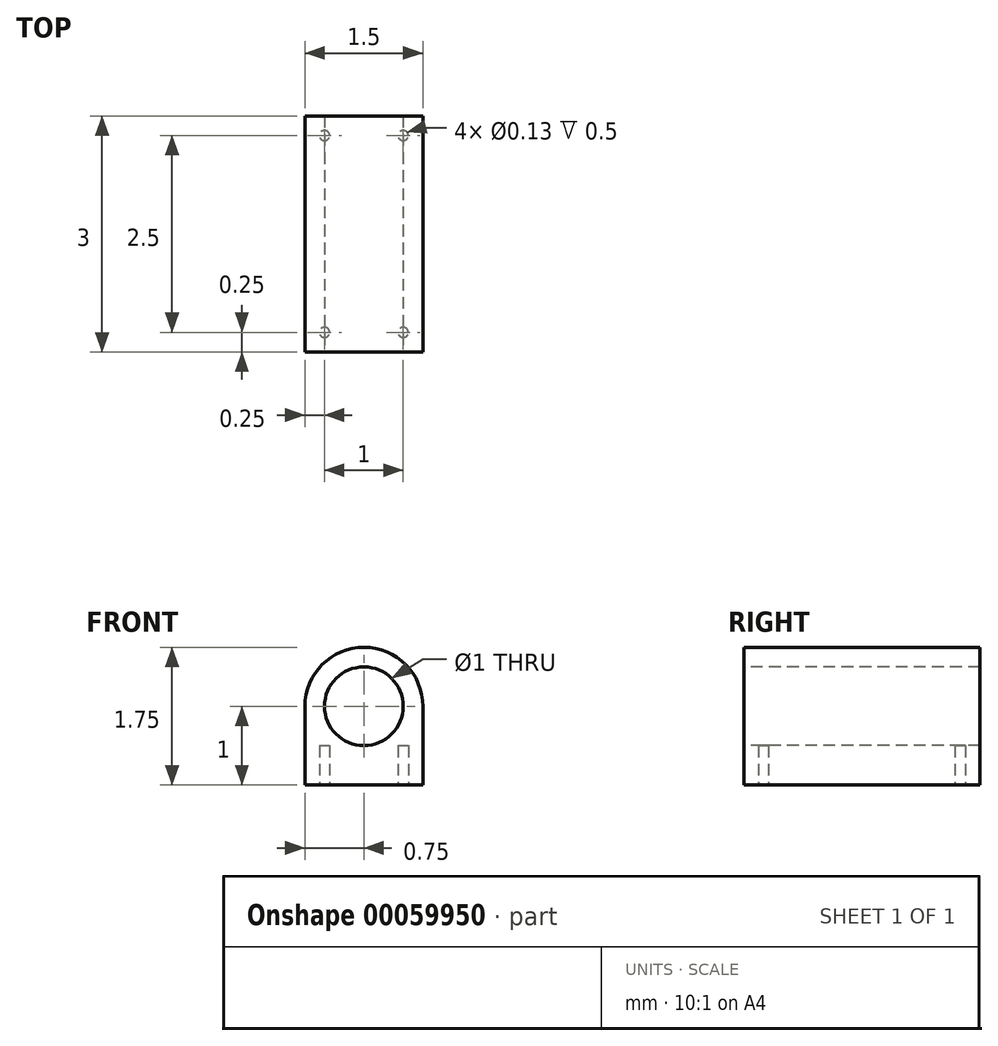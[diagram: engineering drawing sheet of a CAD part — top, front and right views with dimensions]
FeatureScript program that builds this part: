
annotation { "Feature Type Name" : "Feature", "Feature Type Description" : "" }
export const myFeature = defineFeature(function(context is Context, id is Id, definition is map)
    precondition{}
    {
        {
            var Q0;
            Q0=qCreatedBy(makeId("Front.planeOp"),FACE);
            var sketch = newSketch(context, id + "F0", { "sketchPlane" : qUnion([Q0])});
            skLineSegment(sketch, "E0", {"start": v(0, 0) * mm, "end": v(-0.75, 0) * mm});
            skLineSegment(sketch, "E1", {"start": v(-0.75, 0) * mm, "end": v(-0.75, 1) * mm});
            skArc(sketch, "E2", {"start": v(0.75, 1) * mm, "mid": v(0, 1.75) * mm, "end": v(-0.75, 1) * mm});
            skCircle(sketch, "E3", {"center": v(0, 1) * mm, "radius": 0.25 * mm});
            skLineSegment(sketch, "E4", {"start": v(0, 0) * mm, "end": v(0.75, 0) * mm});
            skLineSegment(sketch, "E5", {"start": v(0.75, 0) * mm, "end": v(0.75, 1) * mm});
            skSolve(sketch);
        }
        {
            var Q0;
            Q0 = qSketchRegion(id + "F0", true);
            extrude(context, id + "F1", {"entities" : qUnion([Q0]), "depth" : 3 * mm});
        }
        {
            var Q0;
            Q0=makeQuery(id+"F1.opExtrude","SWEPT_FACE",FACE,{"disambiguationData":[OSD([sQuery(id+"F0.wireOp",EDGE,"E0"),sQuery(id+"F0.wireOp",EDGE,"E4")])]});
            var sketch = newSketch(context, id + "F2", { "sketchPlane" : qUnion([Q0])});
            skCircle(sketch, "E6", {"center": v(-0.5, 2.75) * mm, "radius": 0.07 * mm});
            skCircle(sketch, "E7", {"center": v(0.5, 2.75) * mm, "radius": 0.07 * mm});
            skCircle(sketch, "E8", {"center": v(0.5, 0.25) * mm, "radius": 0.07 * mm});
            skCircle(sketch, "E9", {"center": v(-0.5, 0.25) * mm, "radius": 0.07 * mm});
            skSolve(sketch);
        }
        {
            var Q0;
            Q0 = qSketchRegion(id + "F2", true);
            extrude(context, id + "F3", {"entities" : qUnion([Q0]), "operationType" : NewBodyOperationType.REMOVE, "oppositeDirection" : true, "depth" : 0.5 * mm});
        }
        {
            var Q0;
            Q0=makeQuery(id+"F1.opExtrude","CAP_FACE",FACE,{"disambiguationData":[OSD([sQuery(id+"F0.wireOp",EDGE,"E0"),sQuery(id+"F0.wireOp",EDGE,"E1"),sQuery(id+"F0.wireOp",EDGE,"E2"),sQuery(id+"F0.wireOp",EDGE,"E3"),sQuery(id+"F0.wireOp",EDGE,"E4"),sQuery(id+"F0.wireOp",EDGE,"E5")])],"isStart":false});
            var sketch = newSketch(context, id + "F4", { "sketchPlane" : qUnion([Q0])});
            skCircle(sketch, "E10", {"center": v(0, 1) * mm, "radius": 0.5 * mm});
            skSolve(sketch);
        }
        {
            var Q0;
            Q0 = qSketchRegion(id + "F4", true);
            extrude(context, id + "F5", {"entities" : qUnion([Q0]), "operationType" : NewBodyOperationType.REMOVE, "endBound" : BoundingType.THROUGH_ALL, "oppositeDirection" : true, "depth" : 25 * mm});
        }
    });
